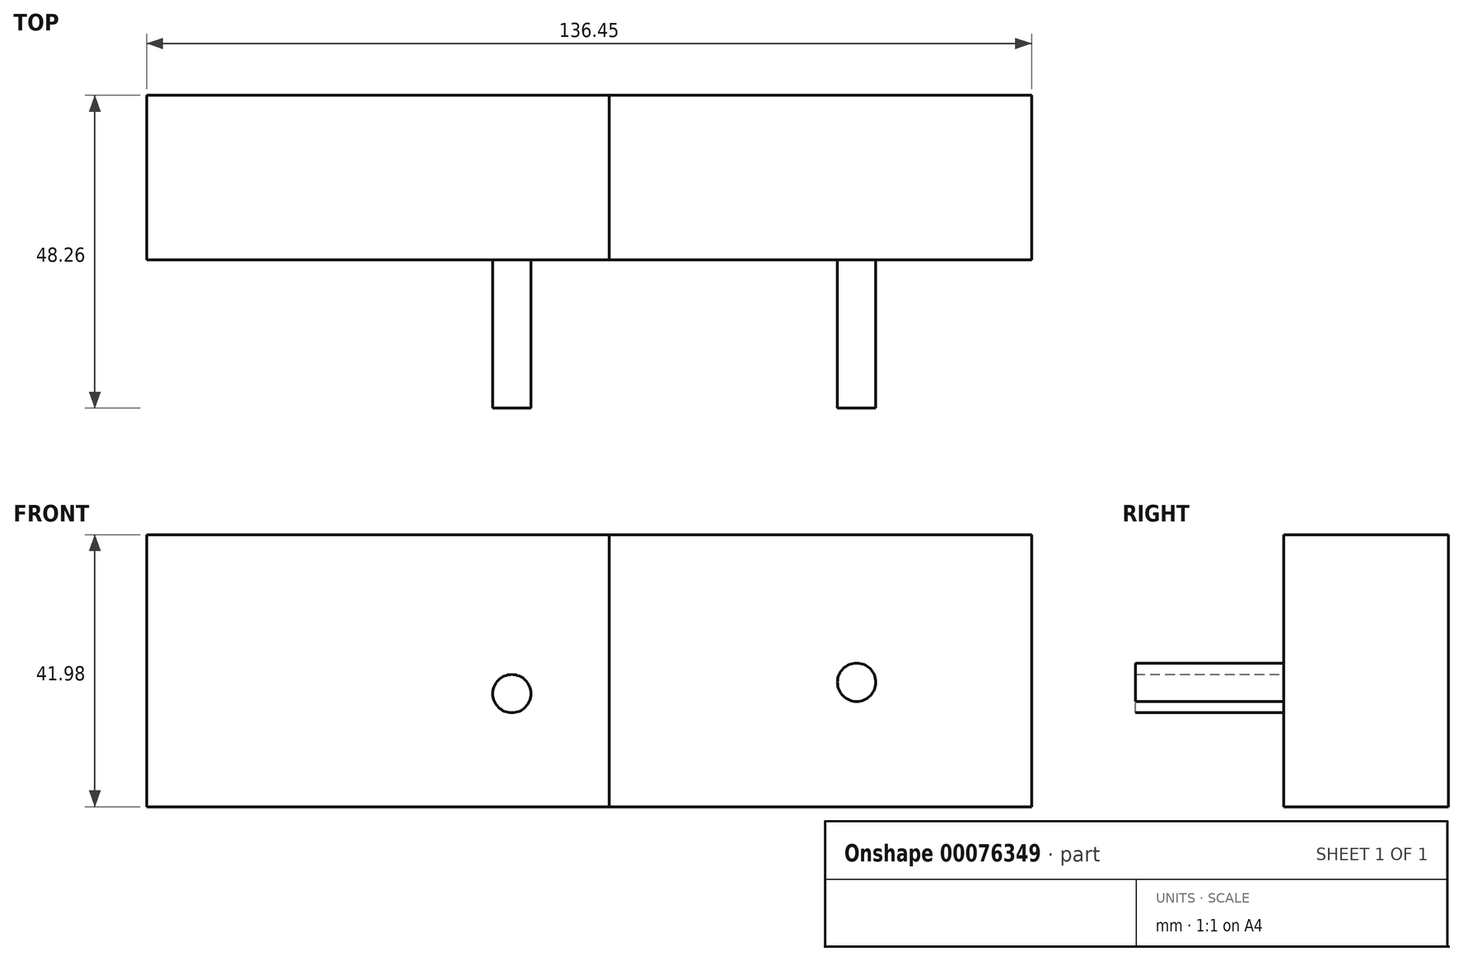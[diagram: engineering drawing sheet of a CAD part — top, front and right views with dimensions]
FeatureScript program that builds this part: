
annotation { "Feature Type Name" : "Feature", "Feature Type Description" : "" }
export const myFeature = defineFeature(function(context is Context, id is Id, definition is map)
    precondition{}
    {
        {
            var Q0;
            Q0=qCreatedBy(makeId("Front.planeOp"),FACE);
            var sketch = newSketch(context, id + "F0", { "sketchPlane" : qUnion([Q0])});
            skLineSegment(sketch, "E0.bottom", {"start": v(0, 0) * mm, "end": v(65.15, 0) * mm});
            skLineSegment(sketch, "E0.top", {"start": v(0, 41.98) * mm, "end": v(65.15, 41.98) * mm});
            skLineSegment(sketch, "E0.left", {"start": v(0, 0) * mm, "end": v(0, 41.98) * mm});
            skLineSegment(sketch, "E0.right", {"start": v(65.15, 0) * mm, "end": v(65.15, 41.98) * mm});
            skSolve(sketch);
        }
        {
            var Q0;
            Q0=makeQuery(id+"F0.imprint","IMPRINT",FACE,{"disambiguationData":[TD([[makeQuery(id+"F0.imprint","IMPRINT",EDGE,{"derivedFrom":sQuery(id+"F0.wireOp",EDGE,"E0.bottom")}),1.0]])]});
            extrude(context, id + "F1", {"entities" : qUnion([Q0]), "depth" : 25.4 * mm});
        }
        {
            var Q0;
            Q0=makeQuery(id+"F1.opExtrude","CAP_FACE",FACE,{"disambiguationData":[OSD([sQuery(id+"F0.wireOp",EDGE,"E0.bottom"),sQuery(id+"F0.wireOp",EDGE,"E0.top"),sQuery(id+"F0.wireOp",EDGE,"E0.left"),sQuery(id+"F0.wireOp",EDGE,"E0.right")])],"isStart":false});
            var sketch = newSketch(context, id + "F2", { "sketchPlane" : qUnion([Q0])});
            skCircle(sketch, "E1", {"center": v(-15, 17.44) * mm, "radius": 2.95 * mm});
            skCircle(sketch, "E2", {"center": v(38.17, 19.2) * mm, "radius": 2.95 * mm});
            skSolve(sketch);
        }
        {
            var Q0;
            Q0 = qSketchRegion(id + "F2", true);
            extrude(context, id + "F3", {"entities" : qUnion([Q0]), "operationType" : NewBodyOperationType.ADD, "depth" : 22.86 * mm});
        }
        {
            var Q0;
            Q0=makeQuery(id+"F1.opExtrude","SWEPT_FACE",FACE,{"disambiguationData":[OSD([sQuery(id+"F0.wireOp",EDGE,"E0.left")])]});
            extrude(context, id + "F4", {"entities" : qUnion([Q0]), "depth" : 71.3 * mm});
        }
    });
